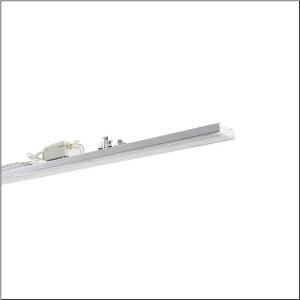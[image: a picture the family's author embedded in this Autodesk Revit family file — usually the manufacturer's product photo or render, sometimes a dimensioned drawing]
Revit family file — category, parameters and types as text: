
# Revit family: licross_11_recessed_ho_51te12dv4m2m3s
name_source: partatom
category: Lighting Fixtures
units: mm (PartAtom-declared; Revit-internal decimal feet)

## family parameters
Cut with Voids When Loaded = No
Host = Face
Light Source = No
Part Type = Normal
Room Calculation Point = No
Round Connector Dimension = Use Diameter
Shared = No

## types (1)
- --- (1 x LED, 1010 lm, 5.9 W, 4000K)
    Apparent Load = 6 VA
    CIE Flux Codes = 66 91 98 100 100
    Color Rendering = 80
    Color Temperature = 4000K
    Default Elevation = 1800 mm
    Description = Licross 11 Recessed HO, luminaire insert, of sheet steel, galvanised, coil coated, white, length: 2.250mm, width: 66mm, height: 67mm, LED rated luminous flux: 27.150lm, light colour: 840, SDCM (Standard Deviation of Colour Matching)MacAdam ≤ 2 SDCM (initial), control gear: DALI 2 (for two DALI lines), with plug, 6-pole, with phase selection, for trunking rail, 14-core, mains connection: 220..240V, AC, 50/60Hz, rated input power: 154W, for trunking rail, 14-core, internal wiring halogen-free, for emergency light function, converter,control gear: single battery element, battery: LiFePO4, 9Ah, primary optical cover: cover, of PMMA, light emission: direct distribution, primary light characteristic: symmetric, protection rating (complete): IP54, insulation class (complete): insulation class I (protective earthing), certification: CE, UKCA, protection symbol: D if used in an environment with non-conductive dust loads with corresponding accessories, impact resistance: IK06, permissible ambient temperature for indoor applications: +5..+35°C, standard: EN 60598-2-22, LABS conformity tested according to VDMA 24364:2018-05, reducing of maximum allowable ambient temperature of 5°C with ceiling mounting, corresponds to IFS (International Featured Standards) requirements for safety and quality in the food industry, The light source and the operating device comply with the requirements of the Ecodesign Regulation (EU) 2019/2020 and are replaceable in accordance with this regulation, packaging unit: 1 piece
    Height = 58 mm
    Lamp = 1 x LED
    Lamp Light Flux = 1010 lm
    Lamp Power = 5.9 W
    Lamp count = 1
    Length = 2250 mm
    Luminous efficacy = 171 lm/W
    Manufacturer = Siteco
    ModVariant = No
    Model = 51TE12DV4M2M3S
    Mounting Place = Ceiling
    Mounting Type = Pendant
    Number of Poles = 1
    OnlyDefault = Yes
    Power Factor = 1
    Product Name = Licross 11 Recessed HO
    Product group = luminaire insert | ceiling pendant
    ProductGroupID = 901
    Protection Class = Protection class I
    Protection Degree = IP 54
    RLX_Detail_Level = 1
    RLX_Emergency_Light_Flux = 0 lm
    RLX_Emergency_Type = 0
    RLX_Emergency_Type_DB = No
    RlxData = <blob elided: 30457 chars, md5=36d30981>
    Socket = socket
    Standby Power = 0 W
    System Light Flux = 1010 lm
    System Power = 6 W
    Type Comments = : emergency light operation: 3 h
    Type Image = l_1296930.jpg
    URL = http://relux.com
    VarID = @adj_091179
    Voltage = 0 V
    Weight = 0.00 kg
    Width = 66 mm

## geometry (parser evidence)
native form markers: Blend x4, Sweep x10
no freeform markers — native parametric forms only
